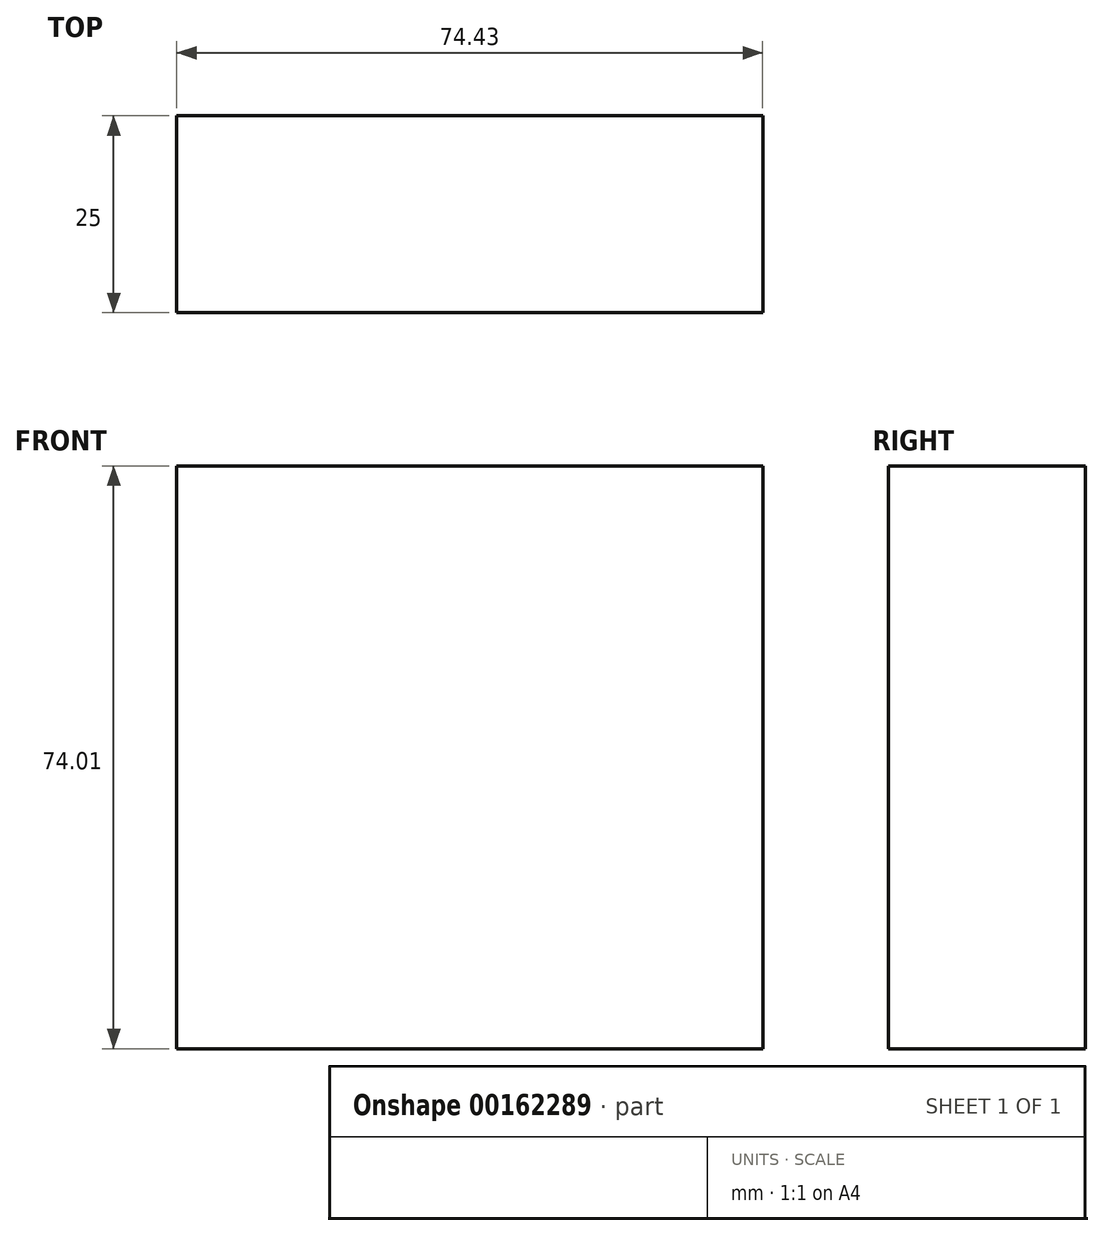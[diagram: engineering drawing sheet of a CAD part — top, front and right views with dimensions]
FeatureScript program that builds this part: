
annotation { "Feature Type Name" : "Feature", "Feature Type Description" : "" }
export const myFeature = defineFeature(function(context is Context, id is Id, definition is map)
    precondition{}
    {
        {
            var Q0;
            Q0=qCreatedBy(makeId("Front.planeOp"),FACE);
            var sketch = newSketch(context, id + "F0", { "sketchPlane" : qUnion([Q0])});
            skLineSegment(sketch, "E0.bottom", {"start": v(0, 0) * mm, "end": v(74.43, 0) * mm});
            skLineSegment(sketch, "E0.top", {"start": v(0, 74.01) * mm, "end": v(74.43, 74.01) * mm});
            skLineSegment(sketch, "E0.left", {"start": v(0, 0) * mm, "end": v(0, 74.01) * mm});
            skLineSegment(sketch, "E0.right", {"start": v(74.43, 0) * mm, "end": v(74.43, 74.01) * mm});
            skSolve(sketch);
        }
        {
            var Q0;
            Q0 = qSketchRegion(id + "F0", true);
            extrude(context, id + "F1", {"entities" : qUnion([Q0]), "endBound" : BoundingType.SYMMETRIC, "depth" : 25 * mm});
        }
    });
